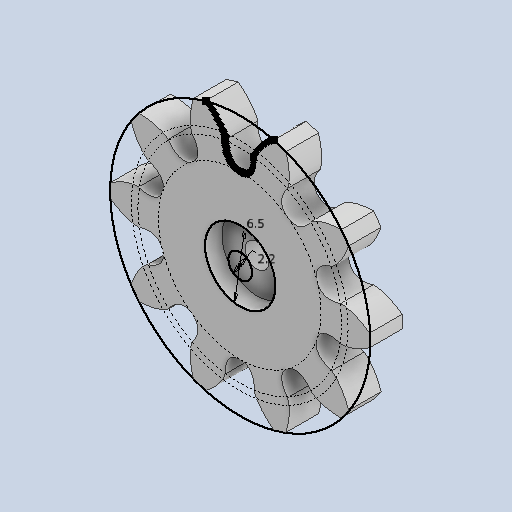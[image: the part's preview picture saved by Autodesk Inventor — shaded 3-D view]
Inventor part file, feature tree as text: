
AUTODESK INVENTOR PART (.ipt)
format: ipt  version: 2023 (Build 270158000, 158)  size: 267,264 bytes
history: native  units: mm
features: extrude x4, other x1, sketch x1, pattern_circular x1
ambient origin geometry x8: Origin, YZ Plane, XZ Plane, XY Plane, X Axis, Y Axis, Z Axis, Center Point
bodies: Solid1 (feature_tree)
feature tree (7):
  other  "pinion_V6"
  sketch  "Sketch1"  dims[d0=3.0mm d1=0.0mm d2=2.2mm d3=2.0mm d4=1.0mm d9=0.0mm d10=0.0mm d11=0.0mm d12=0.0mm d13=100.0mm d14=360.0deg d16=6.5mm d17=1.6mm d18=0.0mm]
  extrude  "Extrusion1"  Depth=1.6mm
  extrude  "Extrusion2"  Depth=1.6mm
  extrude  "Extrusion3"  TaperAngle=0.0deg  [1 undecoded]
  pattern_circular  "Circular Pattern1"  [2 undecoded]
  extrude  "Extrusion4"  Depth=1.6mm TaperAngle=360.0deg
note: 3 required parameter values undecoded (feature->parameter linkage not recoverable at this tier; creation-order binding heuristic only, values carry confidence <= 0.55)
